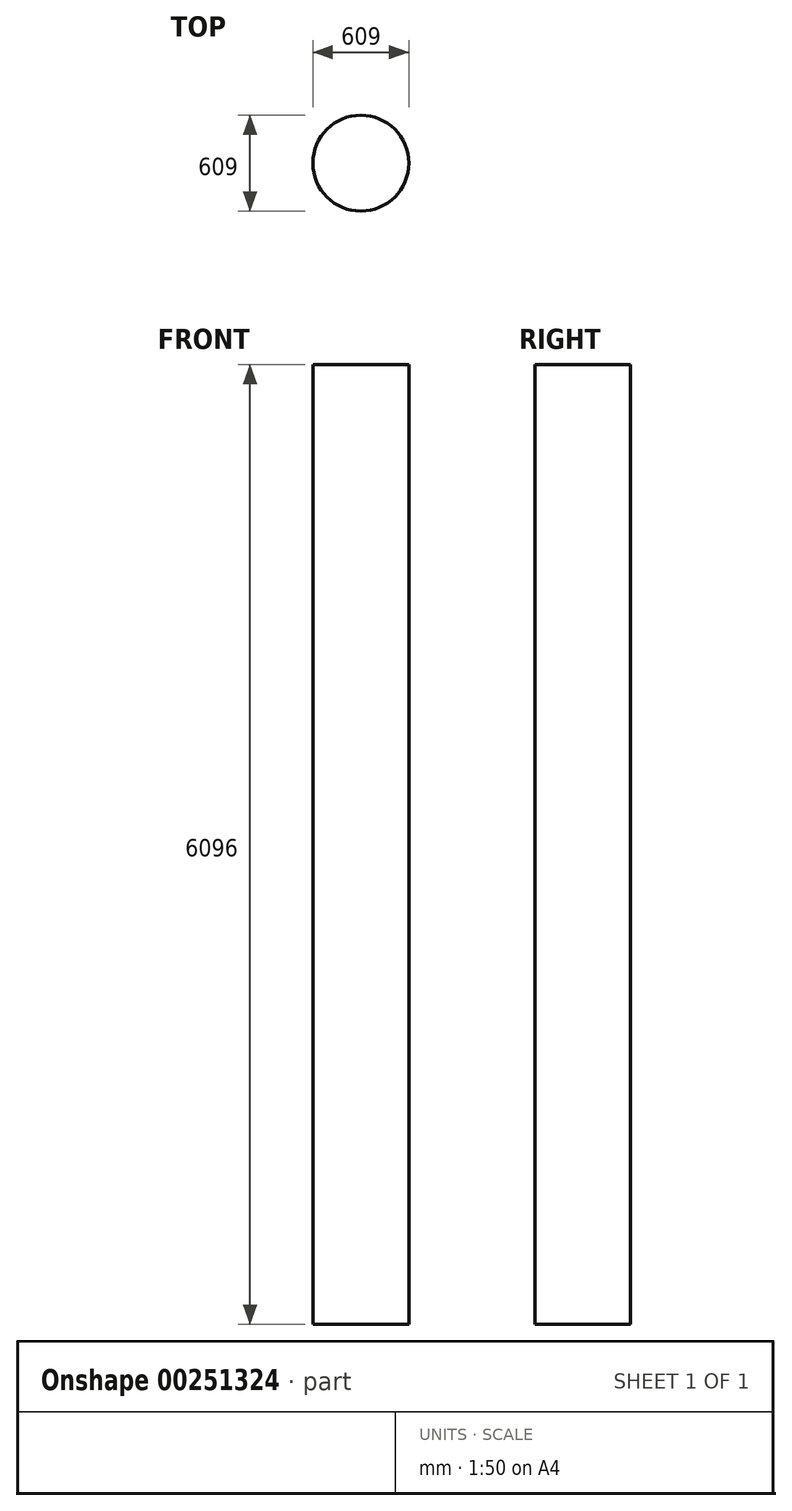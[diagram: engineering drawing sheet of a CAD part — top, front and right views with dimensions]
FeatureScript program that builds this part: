
annotation { "Feature Type Name" : "Feature", "Feature Type Description" : "" }
export const myFeature = defineFeature(function(context is Context, id is Id, definition is map)
    precondition{}
    {
        {
            var Q0;
            Q0=qCreatedBy(makeId("Top.planeOp"),FACE);
            var sketch = newSketch(context, id + "F0", { "sketchPlane" : qUnion([Q0])});
            skCircle(sketch, "E0", {"center": v(0, 0) * mm, "radius": 304.5 * mm});
            skSolve(sketch);
        }
        {
            var Q0;
            Q0=makeQuery(id+"F0.imprint","IMPRINT",FACE,{"disambiguationData":[TD([[makeQuery(id+"F0.imprint","IMPRINT",EDGE,{"derivedFrom":sQuery(id+"F0.wireOp",EDGE,"E0")}),1.0]])]});
            extrude(context, id + "F1", {"entities" : qUnion([Q0]), "depth" : 6096 * mm});
        }
    });
